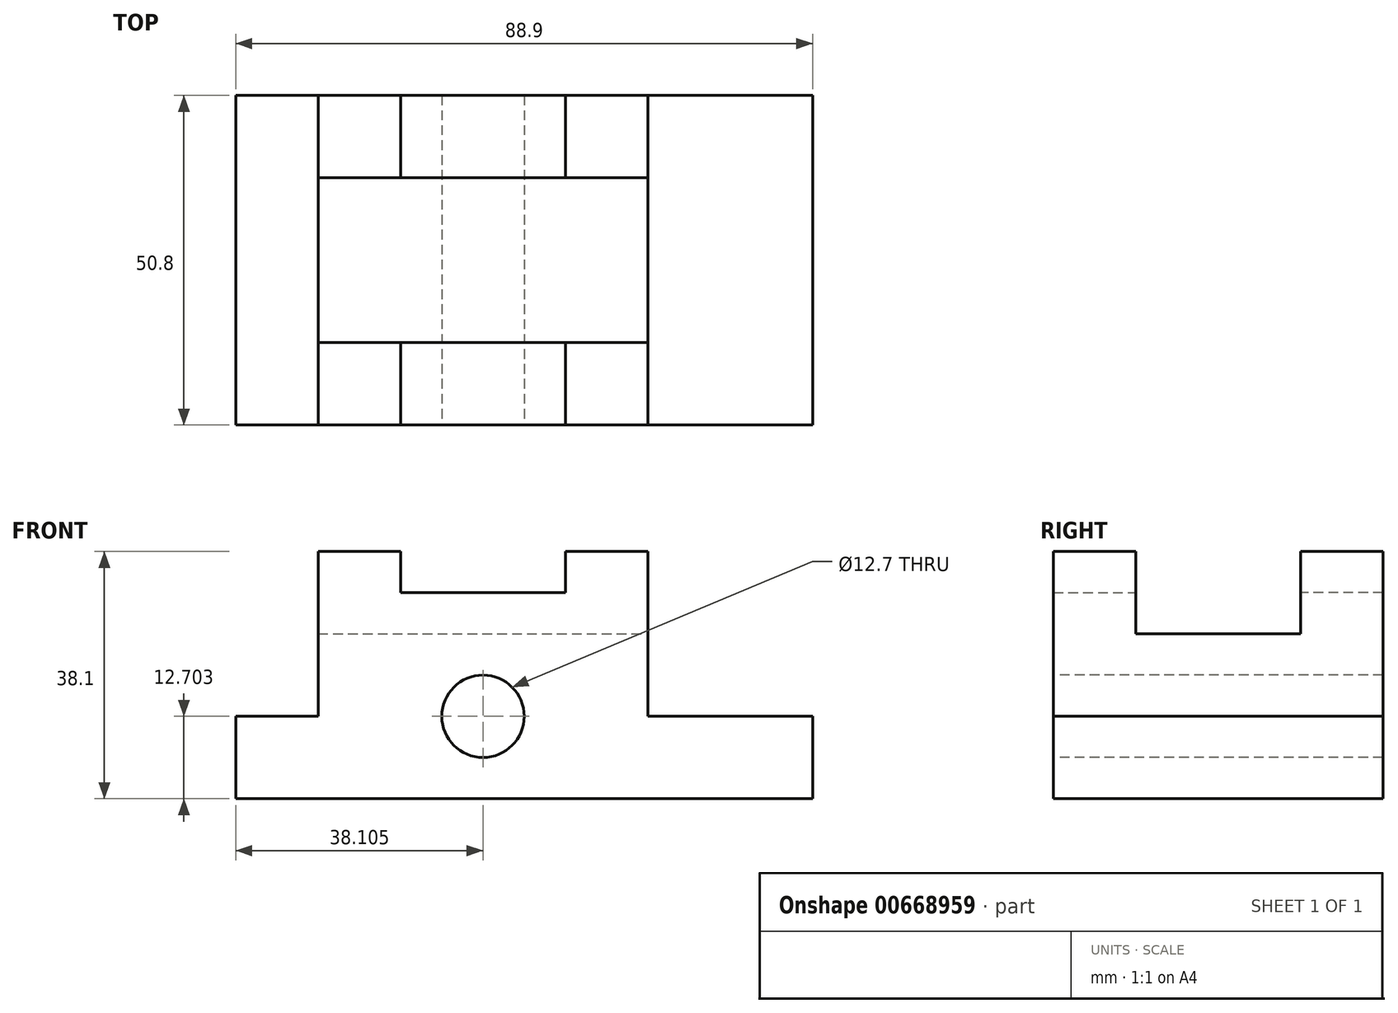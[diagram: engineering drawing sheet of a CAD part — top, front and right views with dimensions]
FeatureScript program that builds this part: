
annotation { "Feature Type Name" : "Feature", "Feature Type Description" : "" }
export const myFeature = defineFeature(function(context is Context, id is Id, definition is map)
    precondition{}
    {
        {
            var Q0;
            Q0=qCreatedBy(makeId("Front.planeOp"),FACE);
            var sketch = newSketch(context, id + "F0", { "sketchPlane" : qUnion([Q0])});
            skLineSegment(sketch, "E0.bottom", {"start": v(-24.13, 20.1) * mm, "end": v(64.77, 20.1) * mm});
            skLineSegment(sketch, "E0.top", {"start": v(-24.13, -18) * mm, "end": v(64.77, -18) * mm});
            skLineSegment(sketch, "E0.left", {"start": v(-24.13, 20.1) * mm, "end": v(-24.13, -18) * mm});
            skLineSegment(sketch, "E0.right", {"start": v(64.77, 20.1) * mm, "end": v(64.77, -18) * mm});
            skSolve(sketch);
        }
        {
            var Q0;
            Q0 = qSketchRegion(id + "F0", true);
            extrude(context, id + "F1", {"entities" : qUnion([Q0]), "depth" : 50.8 * mm, "offsetDistance" : 25.4 * mm});
        }
        {
            var Q0;
            Q0=makeQuery(id+"F1.opExtrude","SWEPT_FACE",FACE,{"disambiguationData":[OSD([sQuery(id+"F0.wireOp",EDGE,"E0.bottom")])]});
            var sketch = newSketch(context, id + "F2", { "sketchPlane" : qUnion([Q0])});
            skLineSegment(sketch, "E1.bottom", {"start": v(-24.13, 0) * mm, "end": v(-11.43, 0) * mm});
            skLineSegment(sketch, "E1.top", {"start": v(-24.13, -50.8) * mm, "end": v(-11.43, -50.8) * mm});
            skLineSegment(sketch, "E1.left", {"start": v(-24.13, 0) * mm, "end": v(-24.13, -50.8) * mm});
            skLineSegment(sketch, "E1.right", {"start": v(-11.43, 0) * mm, "end": v(-11.43, -50.8) * mm});
            skSolve(sketch);
        }
        {
            var Q0;
            Q0 = qSketchRegion(id + "F2", true);
            extrude(context, id + "F3", {"entities" : qUnion([Q0]), "operationType" : NewBodyOperationType.REMOVE, "oppositeDirection" : true, "depth" : 25.4 * mm, "offsetDistance" : 25.4 * mm});
        }
        {
            var Q0;
            Q0=makeQuery(id+"F1.opExtrude","SWEPT_FACE",FACE,{"disambiguationData":[OSD([sQuery(id+"F0.wireOp",EDGE,"E0.bottom")])]});
            var sketch = newSketch(context, id + "F4", { "sketchPlane" : qUnion([Q0])});
            skLineSegment(sketch, "E2.bottom", {"start": v(64.77, 0) * mm, "end": v(39.37, 0) * mm});
            skLineSegment(sketch, "E2.top", {"start": v(64.77, -50.8) * mm, "end": v(39.37, -50.8) * mm});
            skLineSegment(sketch, "E2.left", {"start": v(64.77, 0) * mm, "end": v(64.77, -50.8) * mm});
            skLineSegment(sketch, "E2.right", {"start": v(39.37, 0) * mm, "end": v(39.37, -50.8) * mm});
            skSolve(sketch);
        }
        {
            var Q0;
            Q0 = qSketchRegion(id + "F4", true);
            extrude(context, id + "F5", {"entities" : qUnion([Q0]), "operationType" : NewBodyOperationType.REMOVE, "oppositeDirection" : true, "depth" : 25.4 * mm, "offsetDistance" : 25.4 * mm});
        }
        {
            var Q0;
            Q0=makeQuery(id+"F1.opExtrude","SWEPT_FACE",FACE,{"disambiguationData":[OSD([sQuery(id+"F0.wireOp",EDGE,"E0.bottom")])]});
            var sketch = newSketch(context, id + "F6", { "sketchPlane" : qUnion([Q0])});
            skLineSegment(sketch, "E3.bottom", {"start": v(1.27, -50.8) * mm, "end": v(26.67, -50.8) * mm});
            skLineSegment(sketch, "E3.top", {"start": v(1.27, -38.1) * mm, "end": v(26.67, -38.1) * mm});
            skLineSegment(sketch, "E3.left", {"start": v(1.27, -50.8) * mm, "end": v(1.27, -38.1) * mm});
            skLineSegment(sketch, "E3.right", {"start": v(26.67, -50.8) * mm, "end": v(26.67, -38.1) * mm});
            skSolve(sketch);
        }
        {
            var Q0;
            Q0 = qSketchRegion(id + "F6", true);
            extrude(context, id + "F7", {"entities" : qUnion([Q0]), "operationType" : NewBodyOperationType.REMOVE, "oppositeDirection" : true, "depth" : 6.35 * mm, "offsetDistance" : 25.4 * mm});
        }
        {
            var Q0;
            Q0=makeQuery(id+"F1.opExtrude","SWEPT_FACE",FACE,{"disambiguationData":[OSD([sQuery(id+"F0.wireOp",EDGE,"E0.bottom")])]});
            var sketch = newSketch(context, id + "F8", { "sketchPlane" : qUnion([Q0])});
            skLineSegment(sketch, "E4.bottom", {"start": v(1.27, 0) * mm, "end": v(26.67, 0) * mm});
            skLineSegment(sketch, "E4.top", {"start": v(1.27, -12.7) * mm, "end": v(26.67, -12.7) * mm});
            skLineSegment(sketch, "E4.left", {"start": v(1.27, 0) * mm, "end": v(1.27, -12.7) * mm});
            skLineSegment(sketch, "E4.right", {"start": v(26.67, 0) * mm, "end": v(26.67, -12.7) * mm});
            skSolve(sketch);
        }
        {
            var Q0;
            Q0 = qSketchRegion(id + "F8", true);
            extrude(context, id + "F9", {"entities" : qUnion([Q0]), "operationType" : NewBodyOperationType.REMOVE, "oppositeDirection" : true, "depth" : 6.35 * mm, "offsetDistance" : 25.4 * mm});
        }
        {
            var Q0;
            Q0=makeQuery(id+"F5.boolean.opBoolean","COPY",FACE,{"derivedFrom":makeQuery(id+"F5.opExtrude","SWEPT_FACE",FACE,{"disambiguationData":[OSD([sQuery(id+"F4.wireOp",EDGE,"E2.right")])]})});
            var sketch = newSketch(context, id + "F10", { "sketchPlane" : qUnion([Q0])});
            skLineSegment(sketch, "E5.bottom", {"start": v(-38.1, 20.1) * mm, "end": v(-12.7, 20.1) * mm});
            skLineSegment(sketch, "E5.top", {"start": v(-38.1, 7.4) * mm, "end": v(-12.7, 7.4) * mm});
            skLineSegment(sketch, "E5.left", {"start": v(-38.1, 20.1) * mm, "end": v(-38.1, 7.4) * mm});
            skLineSegment(sketch, "E5.right", {"start": v(-12.7, 20.1) * mm, "end": v(-12.7, 7.4) * mm});
            skSolve(sketch);
        }
        {
            var Q0;
            Q0 = qSketchRegion(id + "F10", true);
            extrude(context, id + "F11", {"entities" : qUnion([Q0]), "operationType" : NewBodyOperationType.REMOVE, "endBound" : BoundingType.THROUGH_ALL, "oppositeDirection" : true, "depth" : 25.4 * mm, "offsetDistance" : 25.4 * mm});
        }
        {
            var Q0;
            Q0=makeQuery(id+"F1.opExtrude","CAP_FACE",FACE,{"disambiguationData":[OSD([sQuery(id+"F0.wireOp",EDGE,"E0.bottom"),sQuery(id+"F0.wireOp",EDGE,"E0.top"),sQuery(id+"F0.wireOp",EDGE,"E0.left"),sQuery(id+"F0.wireOp",EDGE,"E0.right")])],"isStart":false});
            var sketch = newSketch(context, id + "F12", { "sketchPlane" : qUnion([Q0])});
            skCircle(sketch, "E6", {"center": v(13.97, -5.3) * mm, "radius": 6.35 * mm});
            skSolve(sketch);
        }
        {
            var Q0;
            Q0 = qSketchRegion(id + "F12", true);
            extrude(context, id + "F13", {"entities" : qUnion([Q0]), "operationType" : NewBodyOperationType.REMOVE, "endBound" : BoundingType.THROUGH_ALL, "oppositeDirection" : true, "depth" : 25.4 * mm, "offsetDistance" : 25.4 * mm});
        }
    });
